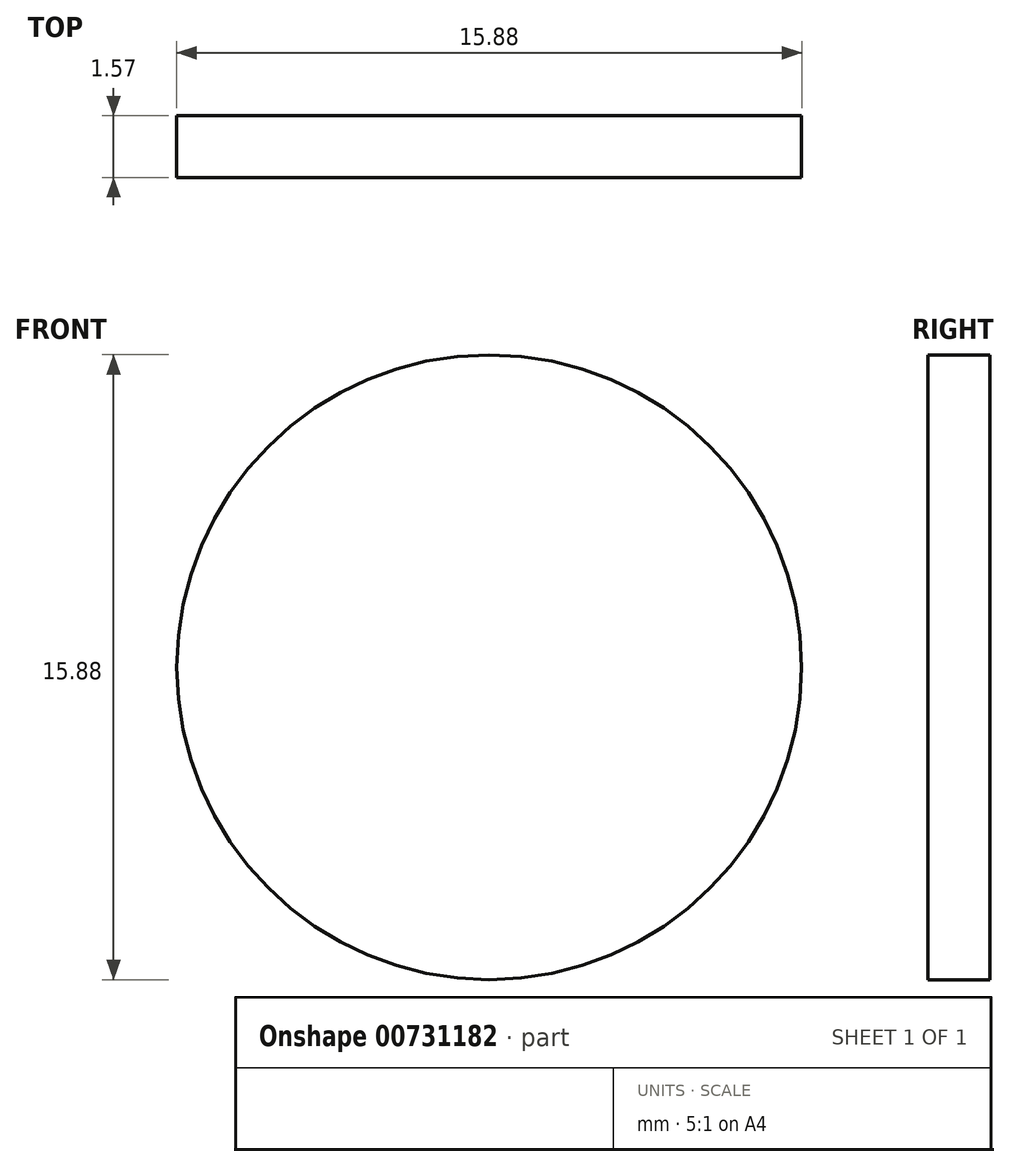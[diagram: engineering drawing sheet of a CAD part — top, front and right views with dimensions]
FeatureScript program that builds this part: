
annotation { "Feature Type Name" : "Feature", "Feature Type Description" : "" }
export const myFeature = defineFeature(function(context is Context, id is Id, definition is map)
    precondition{}
    {
        {
            var Q0;
            Q0=qCreatedBy(makeId("Front.planeOp"),FACE);
            var sketch = newSketch(context, id + "F0", { "sketchPlane" : qUnion([Q0])});
            skCircle(sketch, "E0", {"center": v(0, 0) * mm, "radius": 7.94 * mm});
            skSolve(sketch);
        }
        {
            var Q0;
            Q0=makeQuery(id+"F0.imprint","IMPRINT",FACE,{"disambiguationData":[TD([[makeQuery(id+"F0.imprint","IMPRINT",EDGE,{"derivedFrom":sQuery(id+"F0.wireOp",EDGE,"E0")}),1.0]])]});
            extrude(context, id + "F1", {"entities" : qUnion([Q0]), "oppositeDirection" : true, "depth" : 1.57 * mm, "offsetDistance" : 25.4 * mm});
        }
    });
